# Revit family: 357248xx0--Sanitary_Bidets_Roca_Meridian-Vitreous-china-wall-hung-bidet
name_source: partatom
category: Plumbing Fixtures
units: mm (PartAtom-declared; Revit-internal decimal feet)

## family parameters
Always vertical = No
Cut with Voids When Loaded = No
OmniClass Number = 23.31.23.00
Part Type = Normal
Room Calculation Point = No
Round Connector Dimension = Use Diameter
Shared = No
Work Plane-Based = No

## types (1)
- Meridian Vitreous china wall-hung bidet
    Always visible = Yes
    BIMobject category = Bidets
    Description = Vitreous china wall-hung bidet. Meridian, One single concept for a thousand solutions. One single concept to fulfil any need. The most versatile and global range.
    Design country = Spain
    Diameter = 31.75 mm
    Edition number = 1
    IFC Classification = Sanitary Terminal
    Manufacturer = Roca
    Manufacturer country = Spain
    Manufacturer name = Roca
    Masterformat 2014 Code = 22 41 13.19
    Masterformat 2014 Description = Residential Bidets
    Material 1 = Roca - MERIDIAN - 00 White
    Material main = Vitreous china
    Model = Meridian Vitreous china wall-hung bidet
    OmniClass Code = 23-31 23 00
    OmniClass Description = Bidets
    Product Guid = 8e3640da-4e66-4326-b4ad-248093bd0554
    Product SKU = 357248xx0
    Product data url = https://bimobject.com
    Product group = Meridian
    Product name = Meridian Vitreous china wall-hung bidet
    Product url = http://www.export.roca.com
    QR code = https://www.roca.com
    Technical description = http://www.export.roca.com
    URL = https://www.roca.com
    Uniclass 2015 Code = Pr_40_20_06_11
    Uniclass 2015 Name = Bidets
    Uniformat II Code = D2010
    Uniformat II Description = Plumbing Fixtures
    Youtube clip = https://www.youtube.com

## geometry (parser evidence)
native form markers: Blend x4, Sweep x3
no freeform markers — native parametric forms only
